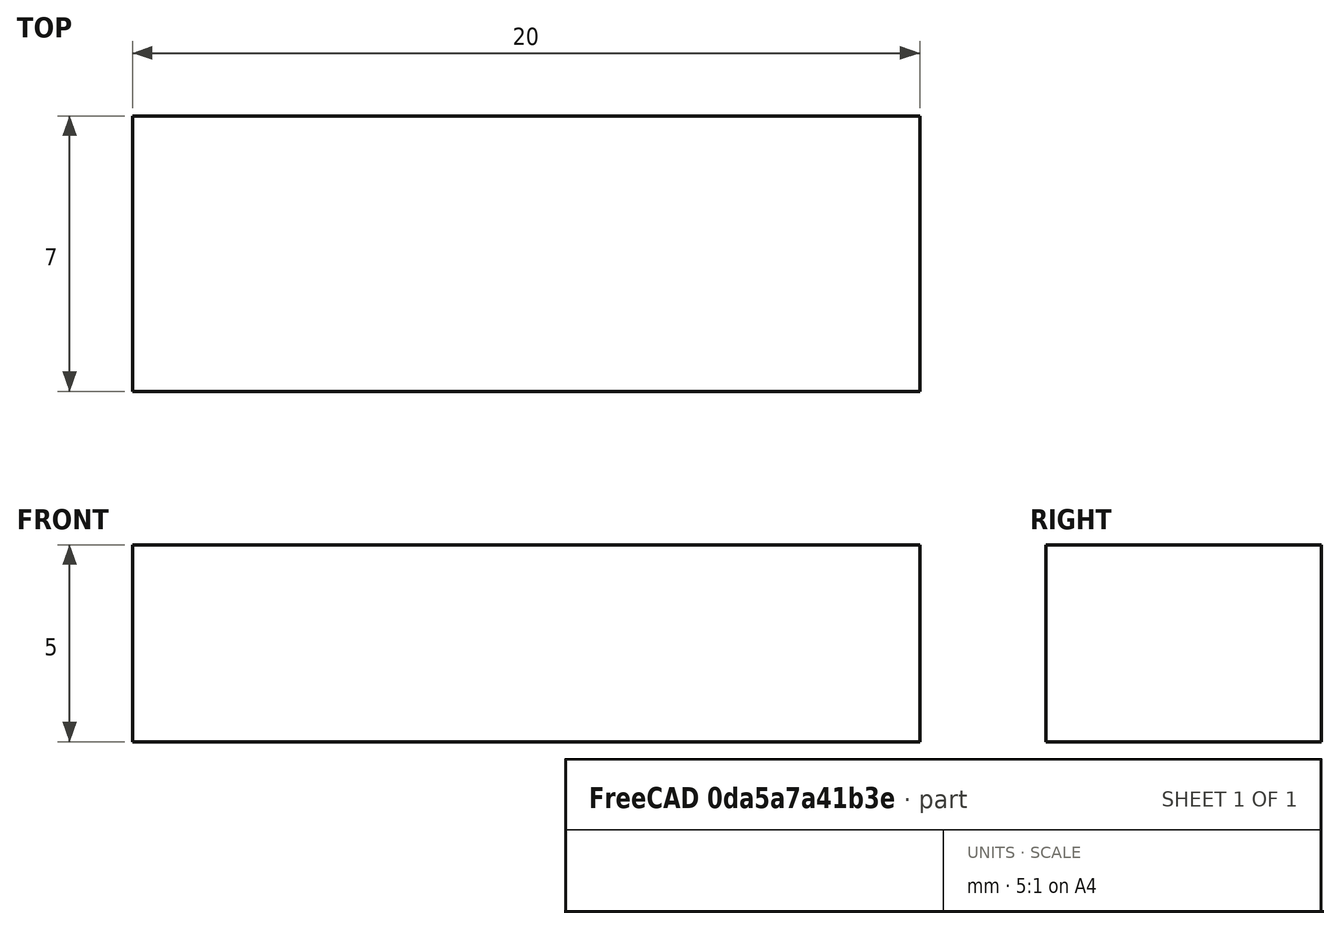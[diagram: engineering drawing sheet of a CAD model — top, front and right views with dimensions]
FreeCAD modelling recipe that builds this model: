
FCSTD DOCUMENT  (FreeCAD 0.19R24276 (Git))
Label: Gt2_roller_support_part_3
License: All rights reserved
LicenseURL: http://en.wikipedia.org/wiki/All_rights_reserved
objects: Sketcher::SketchObject×1, PartDesign::Pad×1, PartDesign::Body×1
note: 4 computed .brp shape members not serialized (recipe doc carries the construction recipe); baked Part::Feature solids carry a one-line shape summary decoded from their .brp

FEATURE [Sketcher::SketchObject] Sketch
  FullyConstrained = true
  MapMode = 5
  Support = -> [XY_Plane]
  sketch-geometry (4):
    g0: LineSegment StartX=0 StartY=0 StartZ=0 EndX=20 EndY=0 EndZ=0
    g1: LineSegment StartX=20 StartY=0 StartZ=0 EndX=20 EndY=7 EndZ=0
    g2: LineSegment StartX=20 StartY=7 StartZ=0 EndX=0 EndY=7 EndZ=0
    g3: LineSegment StartX=0 StartY=7 StartZ=0 EndX=0 EndY=0 EndZ=0
  constraints (11):
    c: Coincident(g0,g1)
    c: Coincident(g1,g2)
    c: Coincident(g2,g3)
    c: Coincident(g3,g0)
    c: Horizontal(g0)
    c: Horizontal(g2)
    c: Vertical(g1)
    c: Vertical(g3)
    c: Coincident(g0,g-1)
    c: DistanceY(g1,g1) = 7
    c: DistanceX(g2,g2) = 20
FEATURE [PartDesign::Pad] Pad
  Direction = (1,1,1)
  Length = 5
  Length2 = 100
  Profile = -> Sketch
  Type = 0
FEATURE [PartDesign::Body] Body
  Group = -> [Sketch,Pad]
  Origin = -> Origin
  Tip = -> Pad
